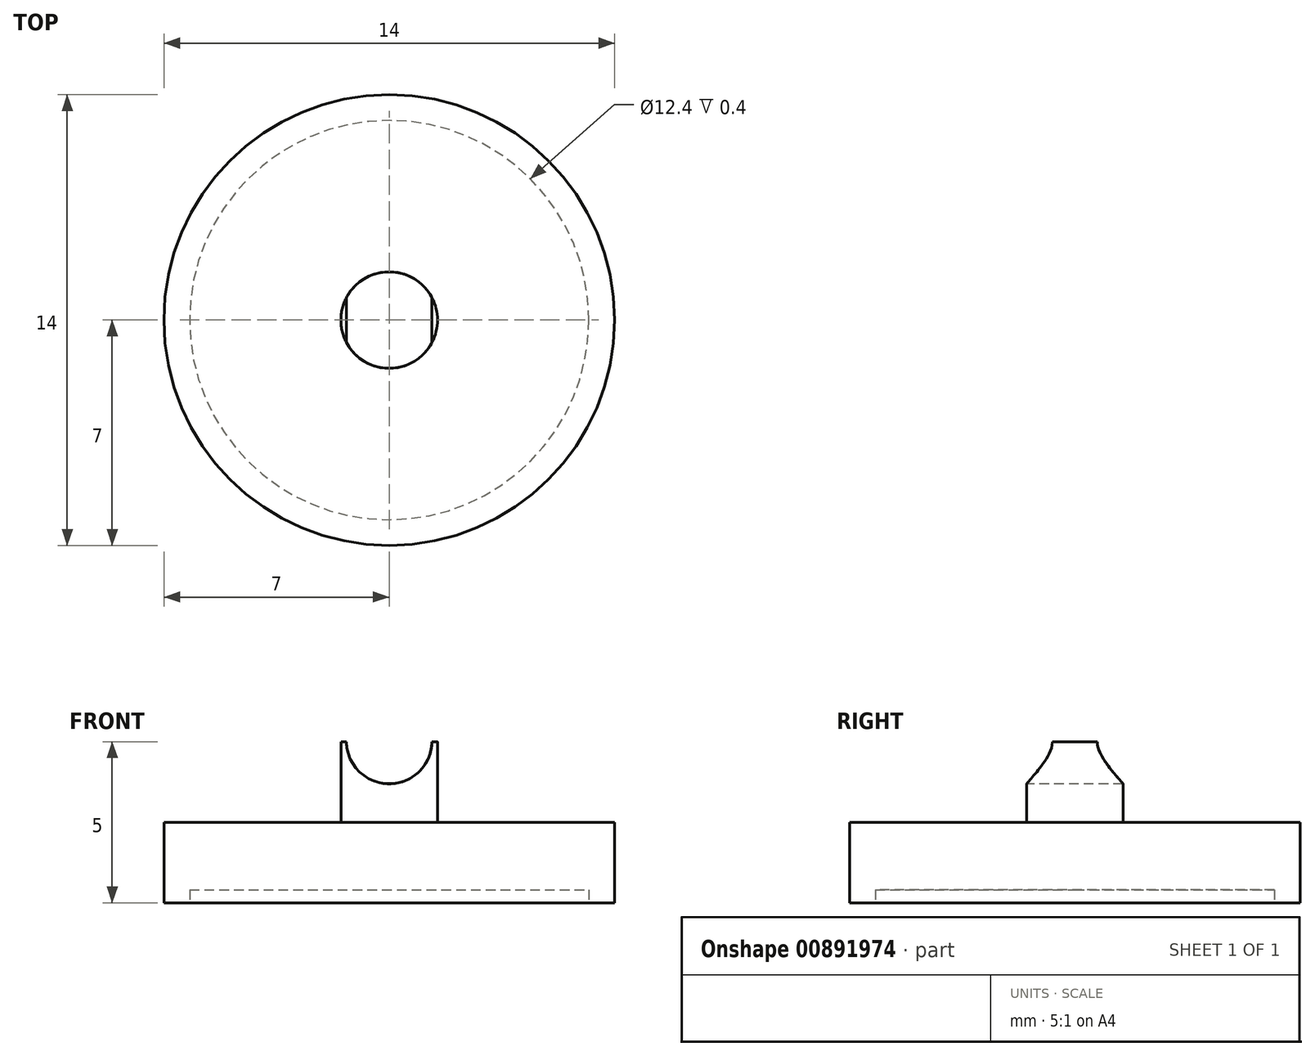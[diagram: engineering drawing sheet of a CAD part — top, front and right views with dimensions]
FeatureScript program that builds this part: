
annotation { "Feature Type Name" : "Feature", "Feature Type Description" : "" }
export const myFeature = defineFeature(function(context is Context, id is Id, definition is map)
    precondition{}
    {
        {
            var Q0;
            Q0=qCreatedBy(makeId("Front.planeOp"),FACE);
            var sketch = newSketch(context, id + "F0", { "sketchPlane" : qUnion([Q0])});
            skLineSegment(sketch, "E0.right", {"start": v(7, 0) * mm, "end": v(7, -2.5) * mm});
            skLineSegment(sketch, "E1.top", {"start": v(0, -2.1) * mm, "end": v(6.2, -2.1) * mm});
            skLineSegment(sketch, "E1.right", {"start": v(6.2, -2.5) * mm, "end": v(6.2, -2.1) * mm});
            skLineSegment(sketch, "E2", {"start": v(6.2, -2.5) * mm, "end": v(7, -2.5) * mm});
            skLineSegment(sketch, "E3", {"start": v(0, 0) * mm, "end": v(0, -2.1) * mm});
            skLineSegment(sketch, "E4", {"start": v(7, 0) * mm, "end": v(7, -1.05) * mm});
            skPoint(sketch, "E4.endSnap0", {"position": v(0, -1.05) * mm});
            skLineSegment(sketch, "E5.top", {"start": v(0, 2.5) * mm, "end": v(1.5, 2.5) * mm});
            skLineSegment(sketch, "E5.left", {"start": v(0, 0) * mm, "end": v(0, 2.5) * mm});
            skLineSegment(sketch, "E5.right", {"start": v(1.5, 0) * mm, "end": v(1.5, 2.5) * mm});
            skLineSegment(sketch, "E6", {"start": v(1.5, 0) * mm, "end": v(7, 0) * mm});
            skSolve(sketch);
        }
        {
            var Q0;
            Q0=makeQuery(id+"F0.imprint","IMPRINT",FACE,{"disambiguationData":[TD([[makeQuery(id+"F0.imprint","IMPRINT",EDGE,{"derivedFrom":sQuery(id+"F0.wireOp",EDGE,"E0.right")}),-1.0]])]});
            var Q1;
            Q1=sQuery(id+"F0.wireOp",EDGE,"E5.left");
            revolve(context, id + "F1", {"surfaceOperationType" : NewSurfaceOperationType.NEW, "entities" : qUnion([Q0]), "axis" : qUnion([Q1]), "revolveType" : RevolveType.FULL});
        }
        {
            var Q0;
            Q0=qCreatedBy(makeId("Front.planeOp"),FACE);
            var sketch = newSketch(context, id + "F2", { "sketchPlane" : qUnion([Q0])});
            skCircle(sketch, "E7", {"center": v(0, 2.52) * mm, "radius": 1.33 * mm});
            skSolve(sketch);
        }
        {
            var Q0;
            Q0=qSketchRegion(id+"F2",true);
            extrude(context, id + "F3", {"entities" : qUnion([Q0]), "operationType" : NewBodyOperationType.REMOVE, "endBound" : BoundingType.SYMMETRIC, "oppositeDirection" : true, "depth" : 25 * mm, "offsetDistance" : 25 * mm});
        }
    });
